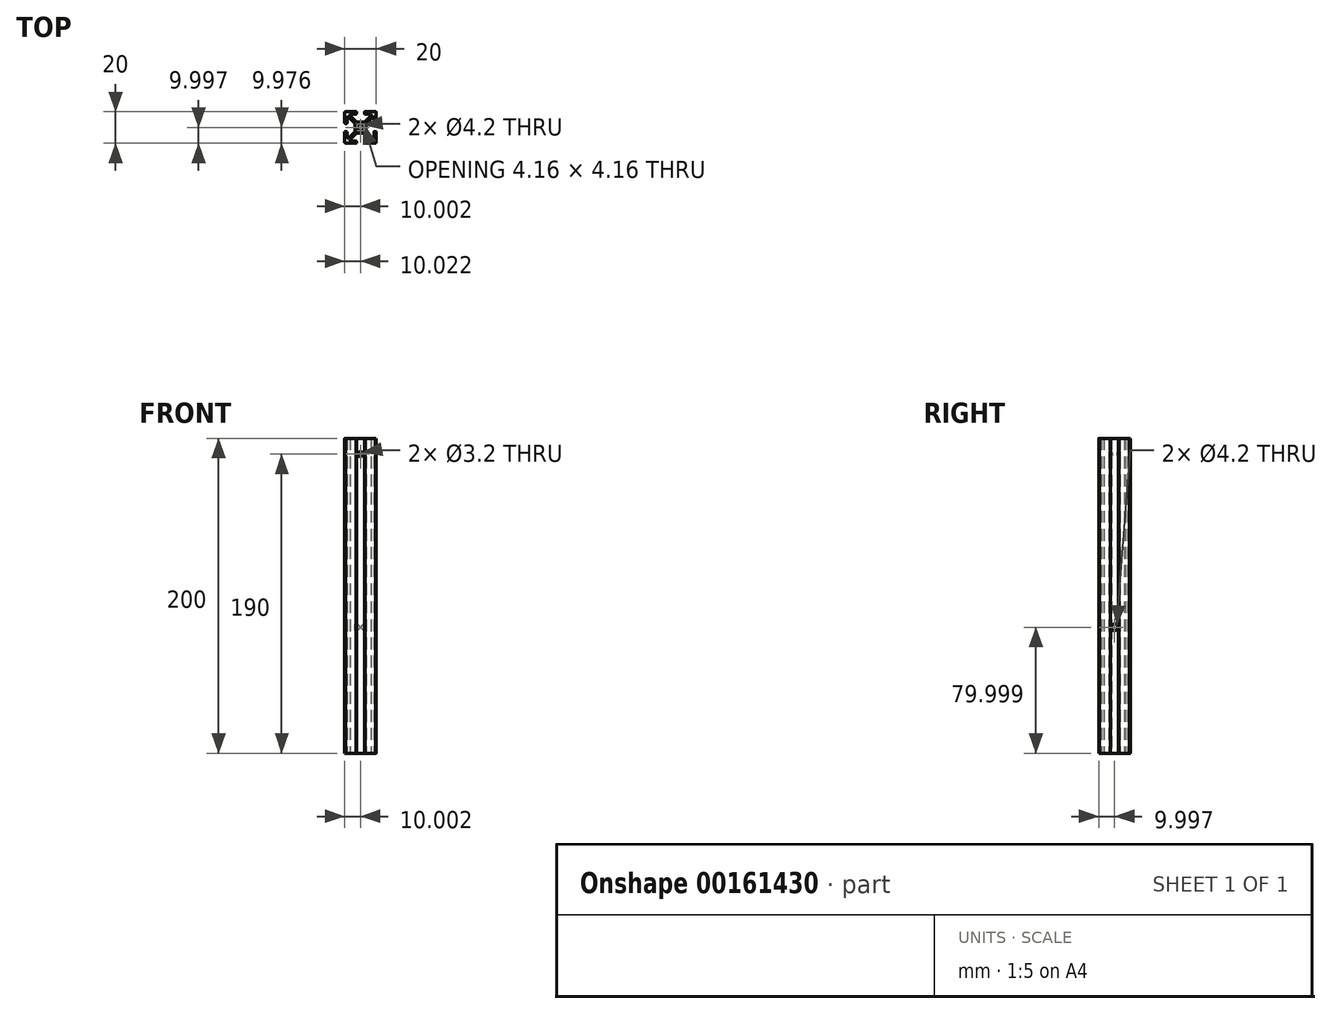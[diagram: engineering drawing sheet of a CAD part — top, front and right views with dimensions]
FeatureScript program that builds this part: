
annotation { "Feature Type Name" : "Feature", "Feature Type Description" : "" }
export const myFeature = defineFeature(function(context is Context, id is Id, definition is map)
    precondition{}
    {
        {
            var Q0;
            Q0=qCreatedBy(makeId("Top.planeOp"),FACE);
            var sketch = newSketch(context, id + "F0", { "sketchPlane" : qUnion([Q0])});
            skLineSegment(sketch, "E0.top", {"start": v(-10.81, -9.52) * mm, "end": v(-10.8, -9.52) * mm});
            skLineSegment(sketch, "E0.right", {"start": v(9.19, 10.48) * mm, "end": v(9.19, 10.47) * mm});
            skLineSegment(sketch, "E1.bottom", {"start": v(-3.56, 10.48) * mm, "end": v(-10.3, 10.48) * mm});
            skLineSegment(sketch, "E1.top", {"start": v(8.7, -9.52) * mm, "end": v(1.95, -9.52) * mm});
            skLineSegment(sketch, "E1.left", {"start": v(9.2, 9.98) * mm, "end": v(9.2, 3.23) * mm});
            skLineSegment(sketch, "E1.right", {"start": v(-10.8, -2.27) * mm, "end": v(-10.8, -9.02) * mm});
            skLineSegment(sketch, "E2", {"start": v(-10.8, 10.48) * mm, "end": v(-10.3, 9.98) * mm});
            skLineSegment(sketch, "E3", {"start": v(9.2, 10.48) * mm, "end": v(8.7, 9.98) * mm});
            skCircle(sketch, "E4", {"center": v(-0.8, 0.48) * mm, "radius": 2.1 * mm});
            skLineSegment(sketch, "E5.left", {"start": v(-3.3, 10.23) * mm, "end": v(-3.3, 9.23) * mm});
            skLineSegment(sketch, "E5.right", {"start": v(1.7, 10.23) * mm, "end": v(1.7, 9.23) * mm});
            skLineSegment(sketch, "E6", {"start": v(-4.3, 2.81) * mm, "end": v(-4.3, -1.86) * mm});
            skLineSegment(sketch, "E7", {"start": v(2.7, 2.81) * mm, "end": v(2.7, -1.86) * mm});
            skLineSegment(sketch, "E8", {"start": v(-7.04, -8.02) * mm, "end": v(-3.56, -8.02) * mm});
            skLineSegment(sketch, "E9", {"start": v(-9.3, -2.27) * mm, "end": v(-9.3, -5.76) * mm});
            skLineSegment(sketch, "E10", {"start": v(7.7, 6.7) * mm, "end": v(7.7, 3.23) * mm});
            skLineSegment(sketch, "E11", {"start": v(-7.04, 8.98) * mm, "end": v(-3.56, 8.98) * mm});
            skLineSegment(sketch, "E12.bottom", {"start": v(7.94, 2.98) * mm, "end": v(8.94, 2.98) * mm});
            skLineSegment(sketch, "E12.top", {"start": v(-10.56, -2.02) * mm, "end": v(-9.56, -2.02) * mm});
            skPoint(sketch, "E12.middle", {"position": v(9.2, 0.48) * mm});
            skLineSegment(sketch, "E13", {"start": v(-7.4, 8.12) * mm, "end": v(-3.32, 4.05) * mm});
            skLineSegment(sketch, "E14", {"start": v(1.7, -3.1) * mm, "end": v(5.78, -7.17) * mm});
            skLineSegment(sketch, "E15", {"start": v(5.78, 8.12) * mm, "end": v(1.7, 4.05) * mm});
            skLineSegment(sketch, "E16", {"start": v(-3.32, -3.1) * mm, "end": v(-7.4, -7.17) * mm});
            skArc(sketch, "E17.filletArc", {"start": v(-7.04, 8.98) * mm, "mid": v(-7.5, 8.67) * mm, "end": v(-7.4, 8.12) * mm});
            skPoint(sketch, "E18.newPointB", {"position": v(9.2, 8.98) * mm});
            skArc(sketch, "E18.filletArc", {"start": v(5.78, 8.12) * mm, "mid": v(5.89, 8.67) * mm, "end": v(5.42, 8.98) * mm});
            skArc(sketch, "E19.filletArc", {"start": v(7.7, 6.7) * mm, "mid": v(7.38, 7.17) * mm, "end": v(6.84, 7.06) * mm});
            skArc(sketch, "E20.filletArc", {"start": v(6.84, -6.1) * mm, "mid": v(7.38, -6.22) * mm, "end": v(7.7, -5.76) * mm});
            skArc(sketch, "E21.filletArc", {"start": v(5.42, -8.02) * mm, "mid": v(5.89, -7.71) * mm, "end": v(5.78, -7.17) * mm});
            skArc(sketch, "E22.filletArc", {"start": v(-7.4, -7.17) * mm, "mid": v(-7.5, -7.71) * mm, "end": v(-7.04, -8.02) * mm});
            skArc(sketch, "E23.filletArc", {"start": v(-9.3, -5.76) * mm, "mid": v(-9, -6.22) * mm, "end": v(-8.45, -6.1) * mm});
            skArc(sketch, "E24.filletArc", {"start": v(-8.45, 7.06) * mm, "mid": v(-9.02, 7.16) * mm, "end": v(-9.3, 6.65) * mm});
            skPoint(sketch, "E25.visualSharp", {"position": v(-10.8, 10.48) * mm});
            skArc(sketch, "E25.filletArc", {"start": v(-10.3, 10.48) * mm, "mid": v(-10.66, 10.33) * mm, "end": v(-10.8, 9.98) * mm});
            skPoint(sketch, "E26.visualSharp", {"position": v(9.2, 10.48) * mm});
            skArc(sketch, "E26.filletArc", {"start": v(9.2, 9.98) * mm, "mid": v(9.05, 10.33) * mm, "end": v(8.7, 10.48) * mm});
            skPoint(sketch, "E27.visualSharp", {"position": v(9.2, -9.52) * mm});
            skArc(sketch, "E27.filletArc", {"start": v(8.7, -9.52) * mm, "mid": v(9.05, -9.38) * mm, "end": v(9.2, -9.02) * mm});
            skPoint(sketch, "E28.visualSharp", {"position": v(-10.8, -9.52) * mm});
            skArc(sketch, "E28.filletArc", {"start": v(-10.8, -9.02) * mm, "mid": v(-10.66, -9.38) * mm, "end": v(-10.3, -9.52) * mm});
            skArc(sketch, "E29.filletArc", {"start": v(-3.56, 8.98) * mm, "mid": v(-3.38, 9.05) * mm, "end": v(-3.3, 9.23) * mm});
            skArc(sketch, "E30.filletArc", {"start": v(-9.3, -2.27) * mm, "mid": v(-9.38, -2.1) * mm, "end": v(-9.56, -2.02) * mm});
            skArc(sketch, "E31.filletArc", {"start": v(-3.3, 10.23) * mm, "mid": v(-3.38, 10.4) * mm, "end": v(-3.56, 10.48) * mm});
            skLineSegment(sketch, "E32", {"start": v(1.94, 10.48) * mm, "end": v(8.7, 10.48) * mm});
            skLineSegment(sketch, "E33", {"start": v(5.42, 8.98) * mm, "end": v(1.94, 8.98) * mm});
            skLineSegment(sketch, "E34", {"start": v(-9.3, 6.65) * mm, "end": v(-9.3, 3.23) * mm});
            skLineSegment(sketch, "E35", {"start": v(7.94, -2.02) * mm, "end": v(8.94, -2.02) * mm});
            skPoint(sketch, "E36.visualSharp", {"position": v(1.7, 8.98) * mm});
            skArc(sketch, "E36.filletArc", {"start": v(1.7, 9.23) * mm, "mid": v(1.77, 9.05) * mm, "end": v(1.94, 8.98) * mm});
            skPoint(sketch, "E37.visualSharp", {"position": v(1.7, 10.48) * mm});
            skArc(sketch, "E37.filletArc", {"start": v(1.94, 10.48) * mm, "mid": v(1.77, 10.4) * mm, "end": v(1.7, 10.23) * mm});
            skPoint(sketch, "E38.newPointB", {"position": v(-10.8, 2.98) * mm});
            skArc(sketch, "E38.filletArc", {"start": v(7.7, 3.23) * mm, "mid": v(7.77, 3.05) * mm, "end": v(7.94, 2.98) * mm});
            skLineSegment(sketch, "E39", {"start": v(7.7, -2.27) * mm, "end": v(7.7, -5.76) * mm});
            skPoint(sketch, "E40.visualSharp", {"position": v(7.7, -2.02) * mm});
            skArc(sketch, "E40.filletArc", {"start": v(7.94, -2.02) * mm, "mid": v(7.77, -2.1) * mm, "end": v(7.7, -2.27) * mm});
            skArc(sketch, "E41.filletArc", {"start": v(8.94, 2.98) * mm, "mid": v(9.12, 3.05) * mm, "end": v(9.2, 3.23) * mm});
            skLineSegment(sketch, "E42", {"start": v(9.2, -2.27) * mm, "end": v(9.2, -9.02) * mm});
            skPoint(sketch, "E43.visualSharp", {"position": v(9.2, -2.02) * mm});
            skArc(sketch, "E43.filletArc", {"start": v(9.2, -2.27) * mm, "mid": v(9.12, -2.1) * mm, "end": v(8.94, -2.02) * mm});
            skLineSegment(sketch, "E44", {"start": v(-9.56, 2.98) * mm, "end": v(-10.56, 2.98) * mm});
            skPoint(sketch, "E45.visualSharp", {"position": v(-9.3, 2.98) * mm});
            skArc(sketch, "E45.filletArc", {"start": v(-9.56, 2.98) * mm, "mid": v(-9.38, 3.05) * mm, "end": v(-9.3, 3.23) * mm});
            skPoint(sketch, "E46.newPointA", {"position": v(-10.8, -2.02) * mm});
            skArc(sketch, "E46.filletArc", {"start": v(-10.56, -2.02) * mm, "mid": v(-10.73, -2.1) * mm, "end": v(-10.8, -2.27) * mm});
            skLineSegment(sketch, "E47", {"start": v(-10.8, 3.23) * mm, "end": v(-10.8, 9.98) * mm});
            skArc(sketch, "E48.filletArc", {"start": v(-10.8, 3.23) * mm, "mid": v(-10.73, 3.05) * mm, "end": v(-10.56, 2.98) * mm});
            skPoint(sketch, "E49.newPointB", {"position": v(-3.3, 2.98) * mm});
            skLineSegment(sketch, "E50", {"start": v(6.84, -6.1) * mm, "end": v(2.77, -2.04) * mm});
            skPoint(sketch, "E50.endSnap0", {"position": v(2.7, -0.27) * mm});
            skPoint(sketch, "E51.newPointA", {"position": v(2.7, -1.96) * mm});
            skPoint(sketch, "E51.newPointB", {"position": v(2.7, -9.52) * mm});
            skArc(sketch, "E51.filletArc", {"start": v(2.7, -1.86) * mm, "mid": v(2.71, -1.95) * mm, "end": v(2.77, -2.04) * mm});
            skLineSegment(sketch, "E52", {"start": v(-3.14, -3.02) * mm, "end": v(1.53, -3.02) * mm});
            skArc(sketch, "E53.filletArc", {"start": v(1.7, -3.1) * mm, "mid": v(1.62, -3.04) * mm, "end": v(1.53, -3.02) * mm});
            skArc(sketch, "E54.filletArc", {"start": v(-3.14, -3.02) * mm, "mid": v(-3.24, -3.04) * mm, "end": v(-3.32, -3.1) * mm});
            skLineSegment(sketch, "E55", {"start": v(-8.45, -6.1) * mm, "end": v(-4.38, -2.04) * mm});
            skLineSegment(sketch, "E56", {"start": v(-8.45, 7.06) * mm, "end": v(-4.38, 2.99) * mm});
            skArc(sketch, "E57.filletArc", {"start": v(-4.3, 2.81) * mm, "mid": v(-4.33, 2.9) * mm, "end": v(-4.38, 2.99) * mm});
            skArc(sketch, "E58.filletArc", {"start": v(-4.38, -2.04) * mm, "mid": v(-4.33, -1.95) * mm, "end": v(-4.3, -1.86) * mm});
            skLineSegment(sketch, "E59", {"start": v(6.84, 7.06) * mm, "end": v(2.77, 2.99) * mm});
            skPoint(sketch, "E60.newPointB", {"position": v(2.7, 8.98) * mm});
            skArc(sketch, "E60.filletArc", {"start": v(2.77, 2.99) * mm, "mid": v(2.71, 2.9) * mm, "end": v(2.7, 2.81) * mm});
            skLineSegment(sketch, "E61", {"start": v(-3.14, 3.98) * mm, "end": v(1.53, 3.98) * mm});
            skArc(sketch, "E62.filletArc", {"start": v(-3.32, 4.05) * mm, "mid": v(-3.24, 4) * mm, "end": v(-3.14, 3.98) * mm});
            skArc(sketch, "E63.filletArc", {"start": v(1.53, 3.98) * mm, "mid": v(1.62, 4) * mm, "end": v(1.7, 4.05) * mm});
            skPoint(sketch, "E64.orphan", {"position": v(-3.3, 10.48) * mm});
            skPoint(sketch, "E65.orphan", {"position": v(-0.8, 10.48) * mm});
            skPoint(sketch, "E66.orphan", {"position": v(-10.8, 0.48) * mm});
            skLineSegment(sketch, "E67.trimOffspring", {"start": v(8.7, -9.02) * mm, "end": v(9.2, -9.52) * mm});
            skLineSegment(sketch, "E68.trimOffspring", {"start": v(-10.3, -9.02) * mm, "end": v(-10.8, -9.52) * mm});
            skPoint(sketch, "E69.trimOffspring.end.orphan", {"position": v(-0.8, -9.52) * mm});
            skLineSegment(sketch, "E70", {"start": v(1.7, 9.73) * mm, "end": v(1.7, 9.15) * mm});
            skPoint(sketch, "E70.startSnap0", {"position": v(1.7, 9.73) * mm});
            skLineSegment(sketch, "E71", {"start": v(-3.3, 9.73) * mm, "end": v(-3.3, 9.23) * mm});
            skPoint(sketch, "E72.start.orphan", {"position": v(-3.14, -8.02) * mm});
            skLineSegment(sketch, "E73.trimOffspring", {"start": v(1.95, -8.02) * mm, "end": v(5.42, -8.02) * mm});
            skLineSegment(sketch, "E74.trimOffspring", {"start": v(-3.56, -9.52) * mm, "end": v(-10.3, -9.52) * mm});
            skLineSegment(sketch, "E75.trimOffspring", {"start": v(1.7, -8.27) * mm, "end": v(1.7, -9.27) * mm});
            skLineSegment(sketch, "E76.trimOffspring", {"start": v(-3.3, -8.27) * mm, "end": v(-3.3, -9.27) * mm});
            skArc(sketch, "E77.filletArc", {"start": v(-3.3, -8.27) * mm, "mid": v(-3.38, -8.1) * mm, "end": v(-3.56, -8.02) * mm});
            skPoint(sketch, "E78.visualSharp", {"position": v(1.7, -8.02) * mm});
            skArc(sketch, "E78.filletArc", {"start": v(1.95, -8.02) * mm, "mid": v(1.78, -8.1) * mm, "end": v(1.7, -8.27) * mm});
            skPoint(sketch, "E79.visualSharp", {"position": v(-3.3, -9.52) * mm});
            skArc(sketch, "E79.filletArc", {"start": v(-3.56, -9.52) * mm, "mid": v(-3.38, -9.45) * mm, "end": v(-3.3, -9.27) * mm});
            skPoint(sketch, "E80.visualSharp", {"position": v(1.7, -9.52) * mm});
            skArc(sketch, "E80.filletArc", {"start": v(1.7, -9.27) * mm, "mid": v(1.78, -9.45) * mm, "end": v(1.95, -9.52) * mm});
            skLineSegment(sketch, "E81.trimOffspring", {"start": v(9.19, -2.23) * mm, "end": v(9.19, -9.08) * mm});
            skLineSegment(sketch, "E82.trimOffspring", {"start": v(1.94, -9.52) * mm, "end": v(8.71, -9.52) * mm});
            skLineSegment(sketch, "E83", {"start": v(-10.8, -9.02) * mm, "end": v(-10.8, -2.27) * mm});
            skLineSegment(sketch, "E84", {"start": v(-10.8, 9.98) * mm, "end": v(-10.8, 3.23) * mm});
            skLineSegment(sketch, "E85.trimOffspring", {"start": v(9.19, 10.04) * mm, "end": v(9.19, 3.19) * mm});
            skLineSegment(sketch, "E86.trimOffspring", {"start": v(9.19, -9.52) * mm, "end": v(9.19, -9.52) * mm});
            skLineSegment(sketch, "E87.trimOffspring", {"start": v(-10.33, -9.52) * mm, "end": v(-3.54, -9.52) * mm});
            skSolve(sketch);
        }
        {
            var Q0;
            Q0=makeQuery(id+"F0.imprint","IMPRINT",FACE,{"disambiguationData":[TD([[makeQuery(id+"F0.imprint","IMPRINT",EDGE,{"derivedFrom":sQuery(id+"F0.wireOp",EDGE,"E4")}),-1.0]])]});
            extrude(context, id + "F1", {"entities" : qUnion([Q0]), "depth" : 200 * mm});
        }
        {
            var Q0;
            Q0=makeQuery(id+"F1.opExtrude","SWEPT_FACE",FACE,{"disambiguationData":[OSD([sQuery(id+"F0.wireOp",EDGE,"E7")])]});
            var sketch = newSketch(context, id + "F2", { "sketchPlane" : qUnion([Q0])});
            skPoint(sketch, "E88", {"position": v(0.48, 80) * mm});
            skPoint(sketch, "E89.orphan", {"position": v(0.48, 200) * mm});
            skPoint(sketch, "E90.orphan", {"position": v(2.81, 80) * mm});
            skPoint(sketch, "E91.start.orphan", {"position": v(-1.86, 80) * mm});
            skCircle(sketch, "E92", {"center": v(0.48, 80) * mm, "radius": 2.1 * mm});
            skSolve(sketch);
        }
        {
            var Q0;
            Q0=qSketchRegion(id+"F2",true);
            extrude(context, id + "F3", {"entities" : qUnion([Q0]), "operationType" : NewBodyOperationType.REMOVE, "oppositeDirection" : true, "depth" : 7 * mm});
        }
        {
            var Q0;
            Q0=makeQuery(id+"F1.opExtrude","SWEPT_FACE",FACE,{"disambiguationData":[OSD([sQuery(id+"F0.wireOp",EDGE,"E61")])]});
            var sketch = newSketch(context, id + "F4", { "sketchPlane" : qUnion([Q0])});
            skPoint(sketch, "E93", {"position": v(0.8, 190) * mm});
            skPoint(sketch, "E94.start.orphan", {"position": v(0.8, 200) * mm});
            skCircle(sketch, "E95", {"center": v(0.8, 190) * mm, "radius": 1.6 * mm});
            skSolve(sketch);
        }
        {
            var Q0;
            Q0 = qSketchRegion(id + "F4", true);
            extrude(context, id + "F5", {"entities" : qUnion([Q0]), "operationType" : NewBodyOperationType.REMOVE, "oppositeDirection" : true, "depth" : 7 * mm});
        }
    });
